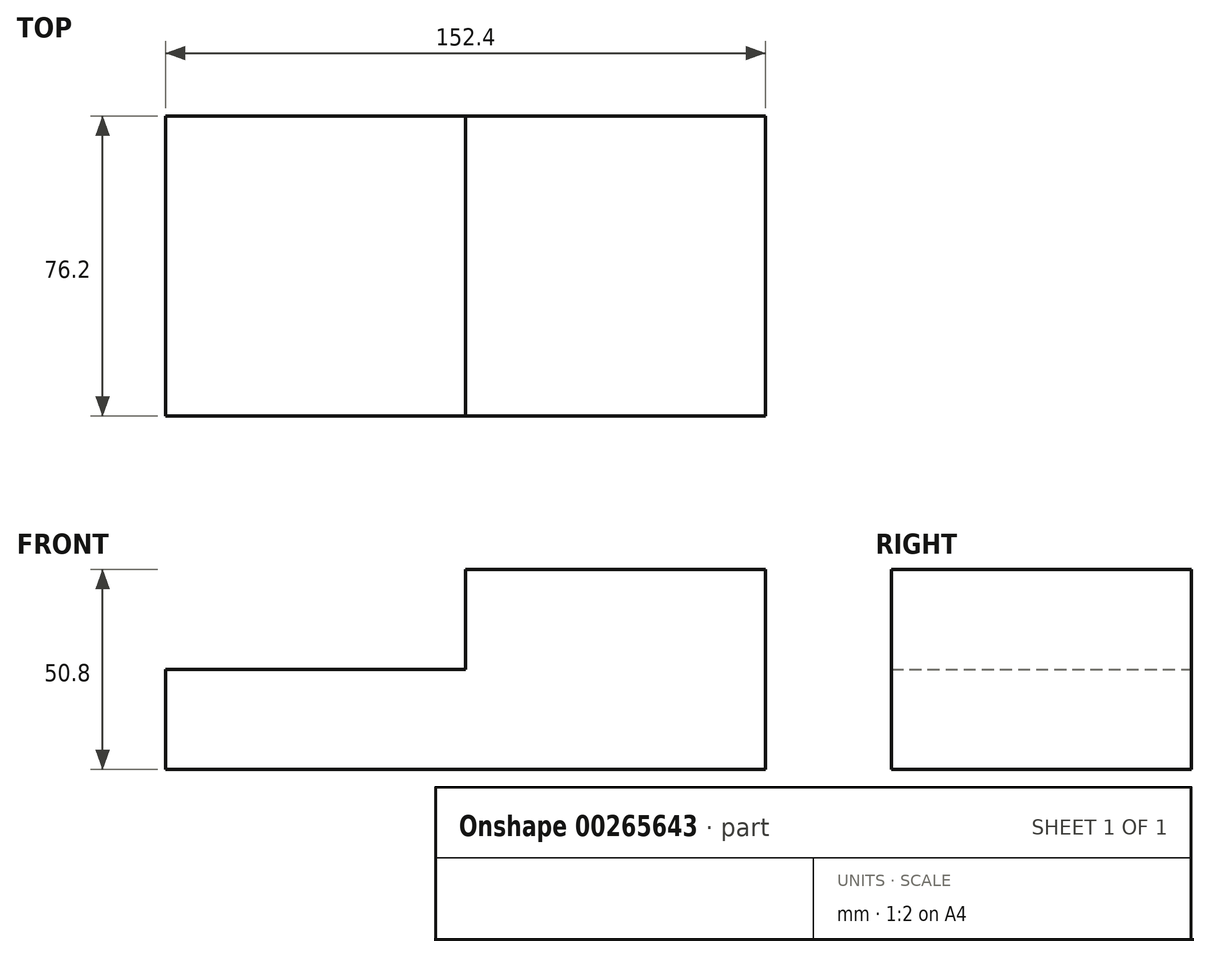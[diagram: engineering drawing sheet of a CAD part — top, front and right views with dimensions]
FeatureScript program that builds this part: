
annotation { "Feature Type Name" : "Feature", "Feature Type Description" : "" }
export const myFeature = defineFeature(function(context is Context, id is Id, definition is map)
    precondition{}
    {
        {
            var Q0;
            Q0=qCreatedBy(makeId("Front.planeOp"),FACE);
            var sketch = newSketch(context, id + "F0", { "sketchPlane" : qUnion([Q0])});
            skLineSegment(sketch, "E0", {"start": v(76.2, 50.8) * mm, "end": v(76.2, 0) * mm});
            skLineSegment(sketch, "E1", {"start": v(76.2, 0) * mm, "end": v(-76.2, 0) * mm});
            skLineSegment(sketch, "E2", {"start": v(-76.2, 0) * mm, "end": v(-76.2, 25.4) * mm});
            skLineSegment(sketch, "E3", {"start": v(-76.2, 25.4) * mm, "end": v(0, 25.4) * mm});
            skLineSegment(sketch, "E4", {"start": v(0, 25.4) * mm, "end": v(0, 50.8) * mm});
            skLineSegment(sketch, "E5", {"start": v(76.2, 50.8) * mm, "end": v(0, 50.8) * mm});
            skSolve(sketch);
        }
        {
            var Q0;
            Q0 = qSketchRegion(id + "F0", true);
            extrude(context, id + "F1", {"entities" : qUnion([Q0]), "depth" : 76.2 * mm});
        }
    });
